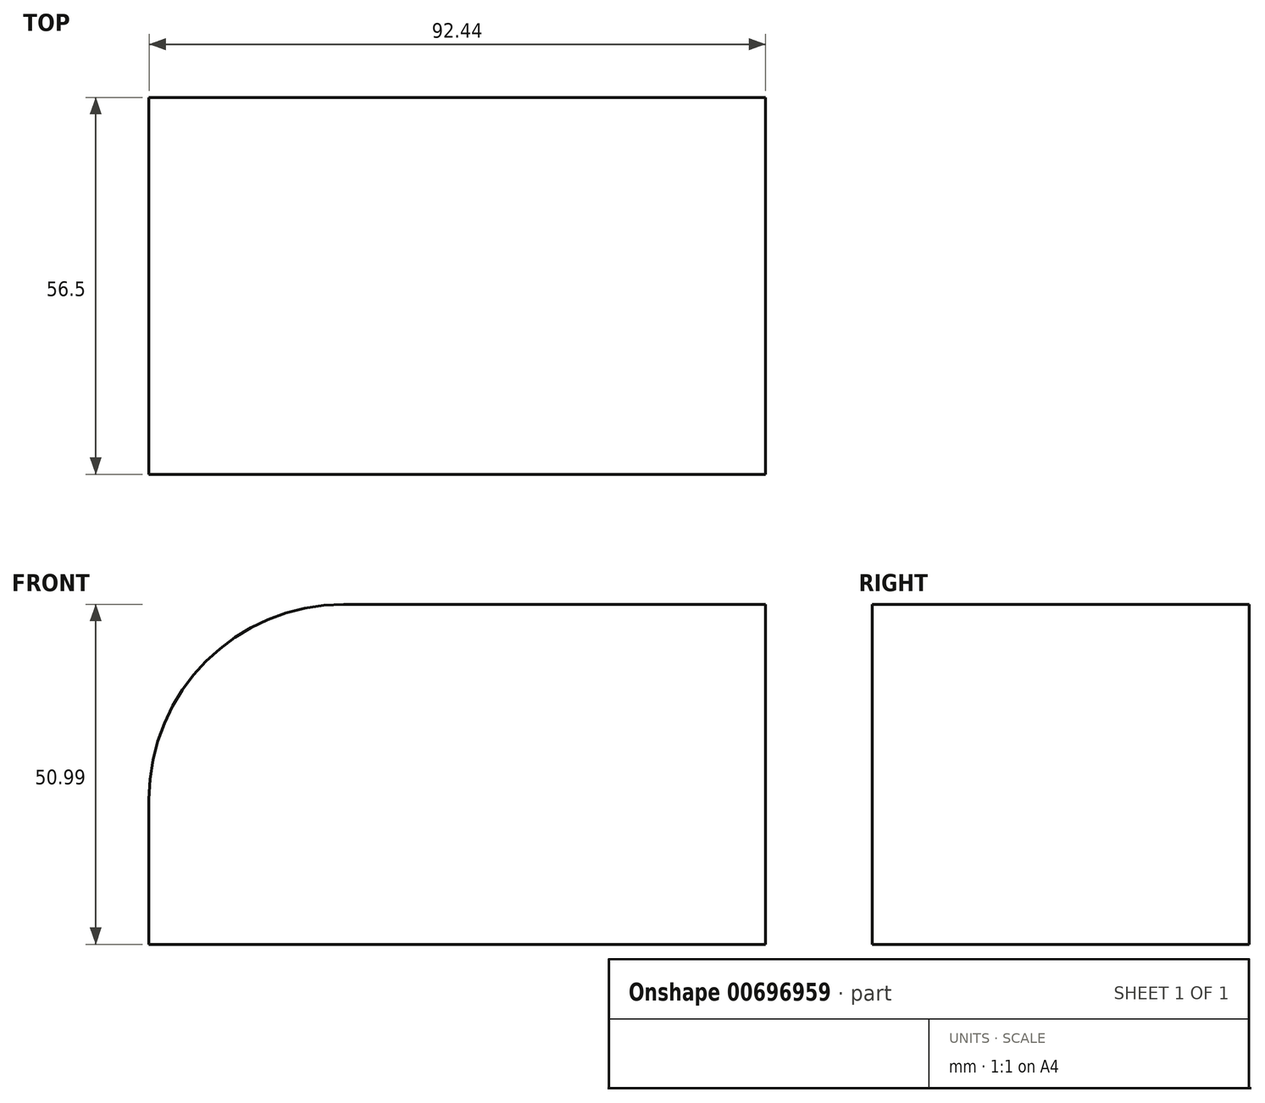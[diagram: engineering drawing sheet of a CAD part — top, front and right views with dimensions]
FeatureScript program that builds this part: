
annotation { "Feature Type Name" : "Feature", "Feature Type Description" : "" }
export const myFeature = defineFeature(function(context is Context, id is Id, definition is map)
    precondition{}
    {
        {
            var Q0;
            Q0=qCreatedBy(makeId("Front.planeOp"),FACE);
            var sketch = newSketch(context, id + "F0", { "sketchPlane" : qUnion([Q0])});
            skLineSegment(sketch, "E0.bottom", {"start": v(46.14, 35.26) * mm, "end": v(-46.3, 35.26) * mm});
            skLineSegment(sketch, "E0.top", {"start": v(46.14, -15.73) * mm, "end": v(-46.3, -15.73) * mm});
            skLineSegment(sketch, "E0.left", {"start": v(46.14, 35.26) * mm, "end": v(46.14, -15.73) * mm});
            skLineSegment(sketch, "E0.right", {"start": v(-46.3, 35.26) * mm, "end": v(-46.3, -15.73) * mm});
            skSolve(sketch);
        }
        {
            var Q0;
            Q0=makeQuery(id+"F0.imprint","IMPRINT",FACE,{"disambiguationData":[TD([[makeQuery(id+"F0.imprint","IMPRINT",EDGE,{"derivedFrom":sQuery(id+"F0.wireOp",EDGE,"E0.bottom")}),1.0]])]});
            extrude(context, id + "F1", {"entities" : qUnion([Q0]), "oppositeDirection" : true, "depth" : 56.5 * mm, "offsetDistance" : 25 * mm});
        }
        {
            var Q0;
            Q0=makeQuery(id+"F1.opExtrude","SWEPT_EDGE",EDGE,{"disambiguationData":[OSD([sQuery(id+"F0.wireOp",EDGE,"E0.bottom"),sQuery(id+"F0.wireOp",EDGE,"E0.right")])]});
            fillet(context, id + "F2", {"entities" : qUnion([Q0]), "radius" : 29.21 * mm, "tangentPropagation" : true, "allowEdgeOverflow" : false});
        }
    });
